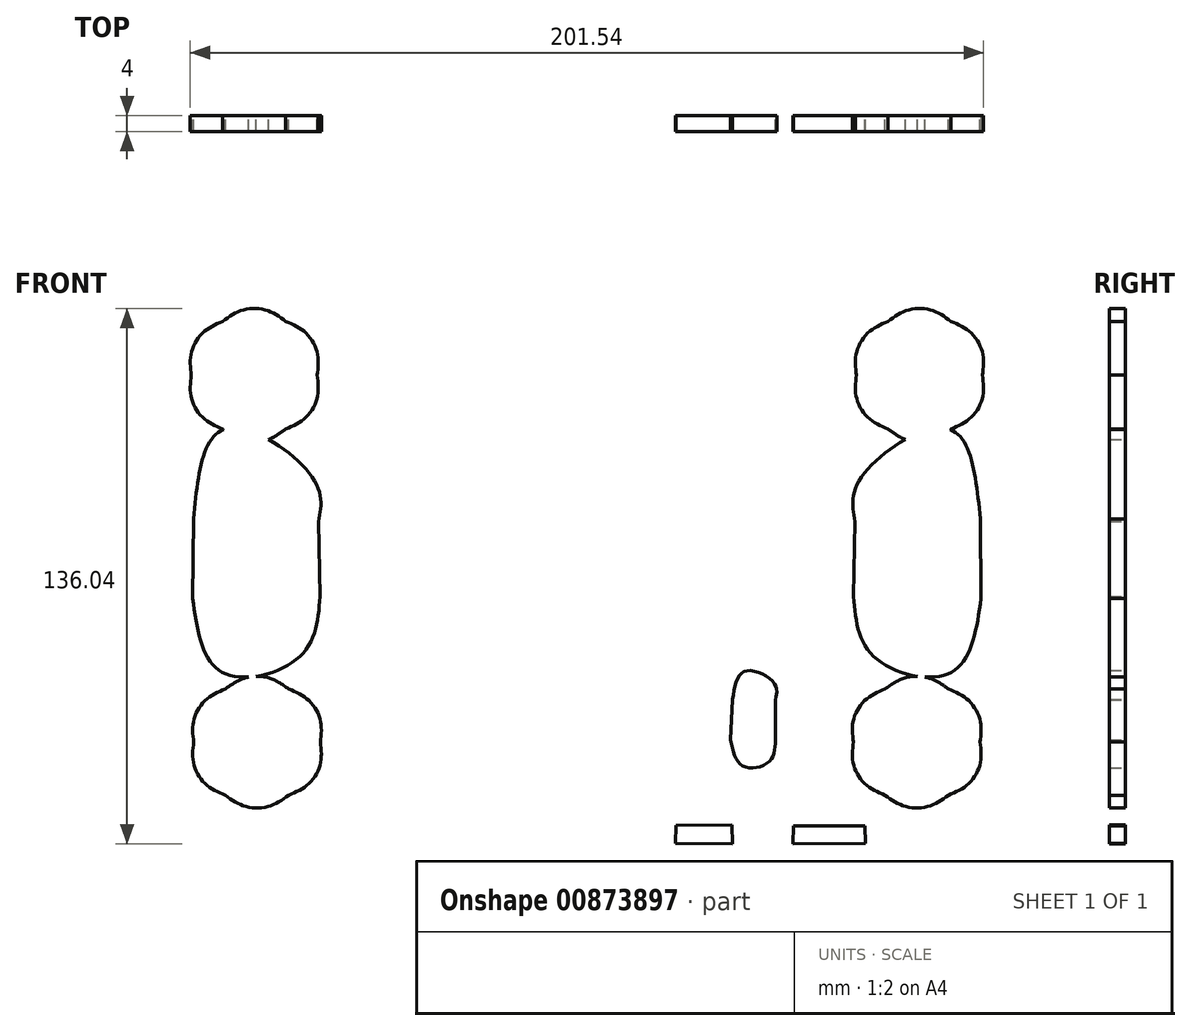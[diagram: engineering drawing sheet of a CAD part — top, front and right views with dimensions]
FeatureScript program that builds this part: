
annotation { "Feature Type Name" : "Feature", "Feature Type Description" : "" }
export const myFeature = defineFeature(function(context is Context, id is Id, definition is map)
    precondition{}
    {
        {
            var Q0;
            Q0=qCreatedBy(makeId("Front.planeOp"),FACE);
            var sketch = newSketch(context, id + "F0", { "sketchPlane" : qUnion([Q0])});
            skLineSegment(sketch, "E0", {"start": v(0, -73.9) * mm, "end": v(87.11, -74.29) * mm});
            skLineSegment(sketch, "E1", {"start": v(87.11, -74.29) * mm, "end": v(101.02, -67.14) * mm});
            skLineSegment(sketch, "E2", {"start": v(101.02, -67.14) * mm, "end": v(105.95, -57.26) * mm});
            skLineSegment(sketch, "E3", {"start": v(105.95, -57.26) * mm, "end": v(106.33, -19.2) * mm});
            skLineSegment(sketch, "E4", {"start": v(106.33, -19.2) * mm, "end": v(108.12, -19.08) * mm});
            skLineSegment(sketch, "E5", {"start": v(108.12, -19.08) * mm, "end": v(108.52, 39.43) * mm});
            skLineSegment(sketch, "E6", {"start": v(108.52, 39.43) * mm, "end": v(106.47, 39.6) * mm});
            skLineSegment(sketch, "E7", {"start": v(106.47, 39.6) * mm, "end": v(106.4, 73.48) * mm});
            skLineSegment(sketch, "E8", {"start": v(106.4, 73.48) * mm, "end": v(92.86, 73.67) * mm});
            skLineSegment(sketch, "E9", {"start": v(92.86, 73.67) * mm, "end": v(92.68, 76.03) * mm});
            skLineSegment(sketch, "E10", {"start": v(92.68, 76.03) * mm, "end": v(77.09, 76.05) * mm});
            skLineSegment(sketch, "E11", {"start": v(77.09, 76.05) * mm, "end": v(77.04, 73.74) * mm});
            skLineSegment(sketch, "E12", {"start": v(77.04, 73.74) * mm, "end": v(54.52, 73.86) * mm});
            skLineSegment(sketch, "E13", {"start": v(54.52, 73.86) * mm, "end": v(54.42, 76.07) * mm});
            skLineSegment(sketch, "E14", {"start": v(54.42, 76.07) * mm, "end": v(0, 76.1) * mm});
            skLineSegment(sketch, "E15", {"start": v(0, 58.28) * mm, "end": v(56.15, 58.5) * mm});
            skLineSegment(sketch, "E16", {"start": v(56.15, 58.5) * mm, "end": v(56.45, -19.08) * mm});
            skLineSegment(sketch, "E17", {"start": v(56.45, -19.08) * mm, "end": v(40.51, -19.17) * mm});
            skLineSegment(sketch, "E18", {"start": v(22.64, -62.17) * mm, "end": v(22.5, -66.81) * mm});
            skLineSegment(sketch, "E19", {"start": v(22.5, -66.81) * mm, "end": v(36.95, -66.88) * mm});
            skLineSegment(sketch, "E20", {"start": v(36.95, -66.88) * mm, "end": v(36.86, -62.1) * mm});
            skLineSegment(sketch, "E21", {"start": v(36.86, -62.1) * mm, "end": v(22.64, -62.17) * mm});
            skLineSegment(sketch, "E22", {"start": v(52.54, -62.3) * mm, "end": v(52.35, -66.86) * mm});
            skLineSegment(sketch, "E23", {"start": v(52.35, -66.86) * mm, "end": v(70.81, -66.8) * mm});
            skLineSegment(sketch, "E24", {"start": v(70.81, -66.8) * mm, "end": v(70.67, -62.26) * mm});
            skLineSegment(sketch, "E25", {"start": v(70.67, -62.26) * mm, "end": v(52.54, -62.3) * mm});
            skLineSegment(sketch, "E26", {"start": v(37.05, -30.14) * mm, "end": v(36.53, -40.42) * mm});
            skLineSegment(sketch, "E27", {"start": v(47.92, -40.42) * mm, "end": v(47.94, -30.26) * mm});
            skLineSegment(sketch, "E28", {"start": v(99.94, 15.72) * mm, "end": v(100.14, -4.53) * mm});
            skLineSegment(sketch, "E29", {"start": v(67.77, -4.03) * mm, "end": v(68.17, 15.01) * mm});
            skFitSpline(sketch, "E30", {"points": [v(40.51, -19.17) * mm, v(36.95, -19.72) * mm, v(31.03, -20.12) * mm, v(28.15, -29.46) * mm]});
            skFitSpline(sketch, "E31", {"points": [v(28.15, -29.46) * mm, v(27.38, -34.88) * mm, v(27.23, -40.46) * mm, v(25.06, -45.54) * mm]});
            skFitSpline(sketch, "E32", {"points": [v(25.06, -45.54) * mm, v(22.54, -50.03) * mm, v(19.6, -53.53) * mm, v(15.17, -56.05) * mm]});
            skFitSpline(sketch, "E33", {"points": [v(15.17, -56.05) * mm, v(10.45, -58.82) * mm, v(5.43, -60.1) * mm, v(0.13, -60.83) * mm]});
            skFitSpline(sketch, "E34", {"points": [v(36.53, -40.42) * mm, v(39.57, -47.05) * mm, v(46.2, -46.08) * mm, v(47.92, -40.42) * mm]});
            skFitSpline(sketch, "E35", {"points": [v(47.94, -30.26) * mm, v(47.6, -26.1) * mm, v(40.19, -23) * mm, v(37.05, -30.14) * mm]});
            skFitSpline(sketch, "E36", {"points": [v(99.9, -41.01) * mm, v(99.9, -46.58) * mm, v(96.83, -51.73) * mm, v(91.85, -54.51) * mm]});
            skFitSpline(sketch, "E37", {"points": [v(91.85, -54.51) * mm, v(86.87, -57.3) * mm, v(80.74, -57.3) * mm, v(75.76, -54.51) * mm]});
            skFitSpline(sketch, "E38", {"points": [v(75.76, -54.51) * mm, v(70.78, -51.73) * mm, v(67.71, -46.58) * mm, v(67.71, -41.01) * mm]});
            skFitSpline(sketch, "E39", {"points": [v(67.71, -41.01) * mm, v(67.71, -35.44) * mm, v(70.78, -30.3) * mm, v(75.76, -27.51) * mm]});
            skFitSpline(sketch, "E40", {"points": [v(75.76, -27.51) * mm, v(80.74, -24.73) * mm, v(86.87, -24.73) * mm, v(91.85, -27.51) * mm]});
            skFitSpline(sketch, "E41", {"points": [v(91.85, -27.51) * mm, v(96.83, -30.3) * mm, v(99.9, -35.44) * mm, v(99.9, -41.01) * mm]});
            skFitSpline(sketch, "E42", {"points": [v(100.52, 52.2) * mm, v(100.52, 46.55) * mm, v(97.47, 41.33) * mm, v(92.51, 38.5) * mm]});
            skFitSpline(sketch, "E43", {"points": [v(92.51, 38.5) * mm, v(87.56, 35.68) * mm, v(81.45, 35.68) * mm, v(76.5, 38.5) * mm]});
            skFitSpline(sketch, "E44", {"points": [v(76.5, 38.5) * mm, v(71.54, 41.33) * mm, v(68.5, 46.55) * mm, v(68.5, 52.2) * mm]});
            skFitSpline(sketch, "E45", {"points": [v(68.5, 52.2) * mm, v(68.5, 57.85) * mm, v(71.54, 63.07) * mm, v(76.5, 65.9) * mm]});
            skFitSpline(sketch, "E46", {"points": [v(76.5, 65.9) * mm, v(81.45, 68.72) * mm, v(87.56, 68.72) * mm, v(92.51, 65.9) * mm]});
            skFitSpline(sketch, "E47", {"points": [v(92.51, 65.9) * mm, v(97.47, 63.07) * mm, v(100.52, 57.85) * mm, v(100.52, 52.2) * mm]});
            skFitSpline(sketch, "E48", {"points": [v(68.17, 15.01) * mm, v(69.44, 25.83) * mm, v(91.65, 38.59) * mm, v(99.94, 15.72) * mm]});
            skFitSpline(sketch, "E49", {"points": [v(100.14, -4.53) * mm, v(92.5, -23.33) * mm, v(72.96, -19.3) * mm, v(67.77, -4.03) * mm]});
            skLineSegment(sketch, "E50", {"start": v(0, 76.1) * mm, "end": v(0, 58.28) * mm});
            skLineSegment(sketch, "E51", {"start": v(0.16, -60.83) * mm, "end": v(0, -60.83) * mm});
            skLineSegment(sketch, "E52", {"start": v(0, -60.83) * mm, "end": v(0, -73.9) * mm});
            skSolve(sketch);
        }
        {
            var Q0;
            Q0 = qSketchRegion(id + "F0", true);
            extrude(context, id + "F1", {"entities" : qUnion([Q0]), "depth" : 4 * mm, "offsetDistance" : 25 * mm});
        }
        {
            var Q0;
            Q0=makeQuery(id+"F1.opExtrude","SWEPT_BODY",BODY,{"disambiguationData":[OSD([sQuery(id+"F0.wireOp",EDGE,"E0"),sQuery(id+"F0.wireOp",EDGE,"E1"),sQuery(id+"F0.wireOp",EDGE,"E2"),sQuery(id+"F0.wireOp",EDGE,"E3"),sQuery(id+"F0.wireOp",EDGE,"E4"),sQuery(id+"F0.wireOp",EDGE,"E5"),sQuery(id+"F0.wireOp",EDGE,"E6"),sQuery(id+"F0.wireOp",EDGE,"E7"),sQuery(id+"F0.wireOp",EDGE,"E8"),sQuery(id+"F0.wireOp",EDGE,"E9"),sQuery(id+"F0.wireOp",EDGE,"E10"),sQuery(id+"F0.wireOp",EDGE,"E11"),sQuery(id+"F0.wireOp",EDGE,"E12"),sQuery(id+"F0.wireOp",EDGE,"E13"),sQuery(id+"F0.wireOp",EDGE,"E14"),sQuery(id+"F0.wireOp",EDGE,"E15"),sQuery(id+"F0.wireOp",EDGE,"E16"),sQuery(id+"F0.wireOp",EDGE,"E17"),sQuery(id+"F0.wireOp",EDGE,"E18"),sQuery(id+"F0.wireOp",EDGE,"E19"),sQuery(id+"F0.wireOp",EDGE,"E20"),sQuery(id+"F0.wireOp",EDGE,"E21"),sQuery(id+"F0.wireOp",EDGE,"E22"),sQuery(id+"F0.wireOp",EDGE,"E23"),sQuery(id+"F0.wireOp",EDGE,"E24"),sQuery(id+"F0.wireOp",EDGE,"E25"),sQuery(id+"F0.wireOp",EDGE,"E26"),sQuery(id+"F0.wireOp",EDGE,"E27"),sQuery(id+"F0.wireOp",EDGE,"E28"),sQuery(id+"F0.wireOp",EDGE,"E29"),sQuery(id+"F0.wireOp",EDGE,"E30"),sQuery(id+"F0.wireOp",EDGE,"E31"),sQuery(id+"F0.wireOp",EDGE,"E32"),sQuery(id+"F0.wireOp",EDGE,"E33"),sQuery(id+"F0.wireOp",EDGE,"E34"),sQuery(id+"F0.wireOp",EDGE,"E35"),sQuery(id+"F0.wireOp",EDGE,"E36"),sQuery(id+"F0.wireOp",EDGE,"E37"),sQuery(id+"F0.wireOp",EDGE,"E38"),sQuery(id+"F0.wireOp",EDGE,"E39"),sQuery(id+"F0.wireOp",EDGE,"E40"),sQuery(id+"F0.wireOp",EDGE,"E41"),sQuery(id+"F0.wireOp",EDGE,"E42"),sQuery(id+"F0.wireOp",EDGE,"E43"),sQuery(id+"F0.wireOp",EDGE,"E44"),sQuery(id+"F0.wireOp",EDGE,"E45"),sQuery(id+"F0.wireOp",EDGE,"E46"),sQuery(id+"F0.wireOp",EDGE,"E47"),sQuery(id+"F0.wireOp",EDGE,"E48"),sQuery(id+"F0.wireOp",EDGE,"E49"),sQuery(id+"F0.wireOp",EDGE,"nMdOlip0-vscO-VJwi-wddo-pfpEHS1aJE3L"),sQuery(id+"F0.wireOp",EDGE,"E50")])]});
            var Q1;
            Q1=qCreatedBy(makeId("Right.planeOp"),FACE);
            mirror(context, id + "F2", {"operationType" : NewBodyOperationType.ADD, "entities" : qUnion([Q0]), "mirrorPlane" : qUnion([Q1])});
        }
    });
